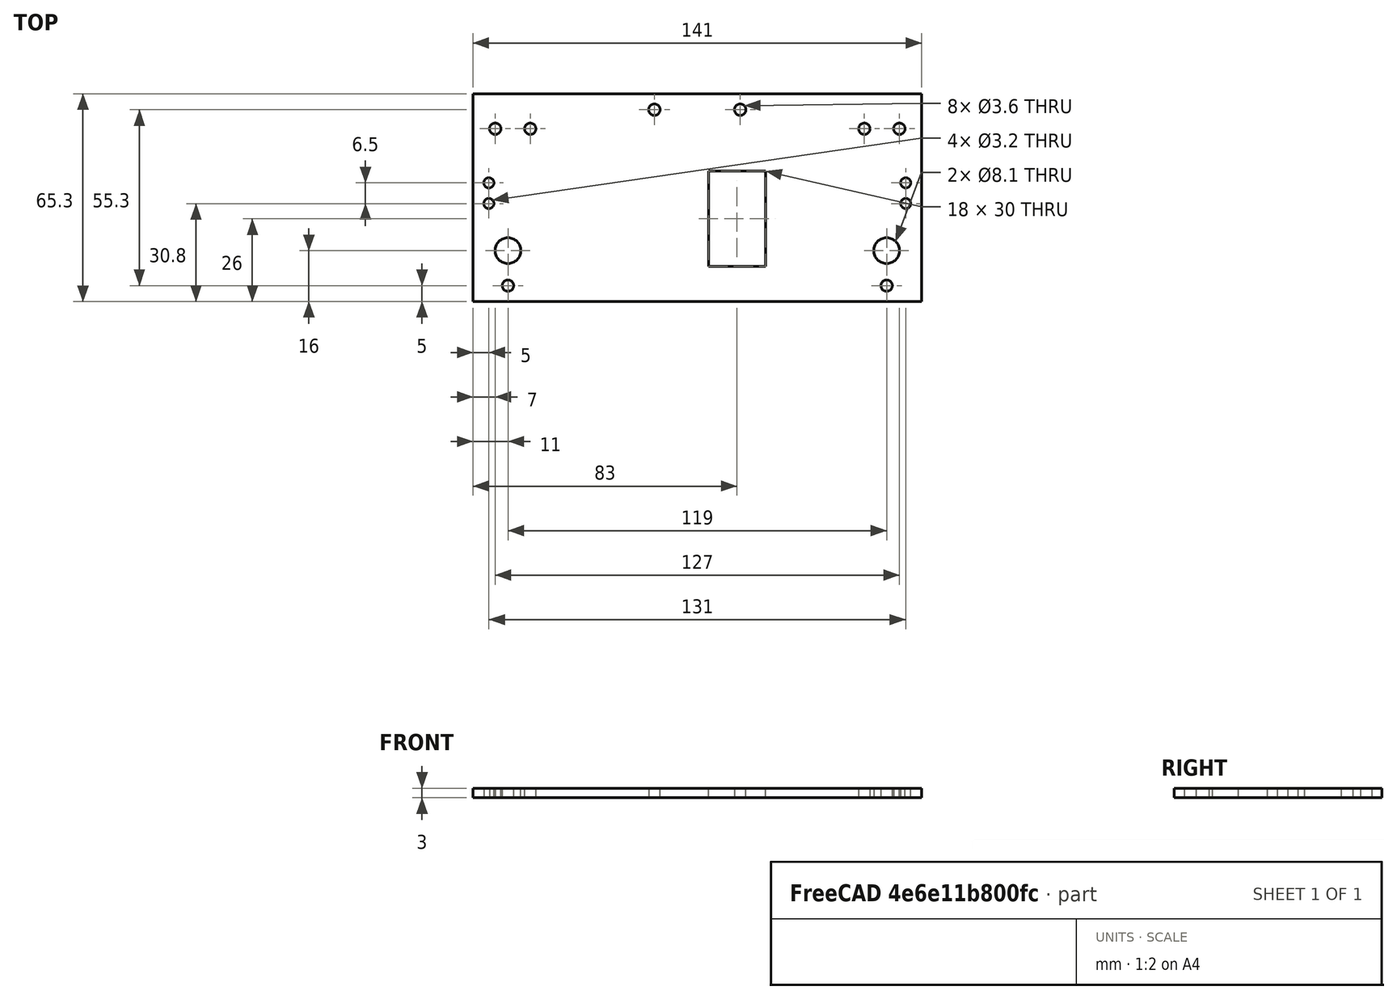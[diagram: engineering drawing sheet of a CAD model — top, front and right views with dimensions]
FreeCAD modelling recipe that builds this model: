
FCSTD DOCUMENT  (FreeCAD 0.16R6706 (Git))
Label: Plate Y Equerda
License: All rights reserved
LicenseURL: http://en.wikipedia.org/wiki/All_rights_reserved
objects: Path::FeaturePython×18, Sketcher::SketchObject×1, PartDesign::Pad×1, Path::FeatureCompoundPython×1
note: 3 computed .brp shape members not serialized (recipe doc carries the construction recipe); baked Part::Feature solids carry a one-line shape summary decoded from their .brp

FEATURE [Sketcher::SketchObject] Sketch
  sketch-geometry (30):
    g0: LineSegment StartX=-141 StartY=65.3 StartZ=0 EndX=0 EndY=65.3 EndZ=0
    g1: LineSegment StartX=0 StartY=65.3 StartZ=0 EndX=0 EndY=0 EndZ=0
    g2: LineSegment StartX=0 StartY=0 StartZ=0 EndX=-141 EndY=0 EndZ=0
    g3: LineSegment StartX=-141 StartY=0 StartZ=0 EndX=-141 EndY=65.3 EndZ=0
    g4: Circle CenterX=-130 CenterY=16 CenterZ=0 NormalX=0 NormalY=0 NormalZ=1 Radius=4.05
    g5: Circle CenterX=-11 CenterY=16 CenterZ=0 NormalX=0 NormalY=0 NormalZ=1 Radius=4.05
    g6: LineSegment [constr] StartX=-130 StartY=16 StartZ=0 EndX=-11 EndY=16 EndZ=0
    g7: LineSegment [constr] StartX=-134 StartY=54.3 StartZ=0 EndX=-123 EndY=54.3 EndZ=0
    g8: Circle CenterX=-134 CenterY=54.3 CenterZ=0 NormalX=0 NormalY=0 NormalZ=1 Radius=1.8
    g9: Circle CenterX=-123 CenterY=54.3 CenterZ=0 NormalX=0 NormalY=0 NormalZ=1 Radius=1.8
    g10: LineSegment [constr] StartX=-18 StartY=54.3 StartZ=0 EndX=-7 EndY=54.3 EndZ=0
    g11: Circle CenterX=-18 CenterY=54.3 CenterZ=0 NormalX=0 NormalY=0 NormalZ=1 Radius=1.8
    g12: Circle CenterX=-7 CenterY=54.3 CenterZ=0 NormalX=0 NormalY=0 NormalZ=1 Radius=1.8
    g13: LineSegment StartX=-67 StartY=41 StartZ=0 EndX=-49 EndY=41 EndZ=0
    g14: LineSegment StartX=-49 StartY=41 StartZ=0 EndX=-49 EndY=11 EndZ=0
    g15: LineSegment StartX=-49 StartY=11 StartZ=0 EndX=-67 EndY=11 EndZ=0
    g16: LineSegment StartX=-67 StartY=11 StartZ=0 EndX=-67 EndY=41 EndZ=0
    g17: LineSegment [constr] StartX=-5 StartY=37.3 StartZ=0 EndX=-5 EndY=30.8 EndZ=0
    g18: Circle CenterX=-5 CenterY=37.3 CenterZ=0 NormalX=0 NormalY=0 NormalZ=1 Radius=1.6
    g19: Circle CenterX=-5 CenterY=30.8 CenterZ=0 NormalX=0 NormalY=0 NormalZ=1 Radius=1.6
    g20: LineSegment [constr] StartX=-136 StartY=37.3 StartZ=0 EndX=-136 EndY=30.8 EndZ=0
    g21: Circle CenterX=-136 CenterY=37.3 CenterZ=0 NormalX=0 NormalY=0 NormalZ=1 Radius=1.6
    g22: Circle CenterX=-136 CenterY=30.8 CenterZ=0 NormalX=0 NormalY=0 NormalZ=1 Radius=1.6
    g23: LineSegment [constr] StartX=-84 StartY=60.3 StartZ=0 EndX=-57 EndY=60.3 EndZ=0
    g24: LineSegment [constr] StartX=-70.5 StartY=60.3 StartZ=0 EndX=-70.5 EndY=65.3 EndZ=0
    g25: Circle CenterX=-84 CenterY=60.3 CenterZ=0 NormalX=0 NormalY=0 NormalZ=1 Radius=1.8
    g26: Circle CenterX=-57 CenterY=60.3 CenterZ=0 NormalX=0 NormalY=0 NormalZ=1 Radius=1.8
    g27: LineSegment [constr] StartX=-130 StartY=5 StartZ=0 EndX=-11 EndY=5 EndZ=0
    g28: Circle CenterX=-130 CenterY=5 CenterZ=0 NormalX=0 NormalY=0 NormalZ=1 Radius=1.8
    g29: Circle CenterX=-11 CenterY=5 CenterZ=0 NormalX=0 NormalY=0 NormalZ=1 Radius=1.8
  constraints (82):
    c: Coincident(g0,g1)
    c: Coincident(g1,g2)
    c: Coincident(g2,g3)
    c: Coincident(g3,g0)
    c: Horizontal(g0)
    c: Horizontal(g2)
    c: Vertical(g1)
    c: Vertical(g3)
    c: Coincident(g1,g-1)
    c: Radius(g4) = 4.05
    c: Equal(g4,g5) = 4.3
    c: Horizontal(g6)
    c: Coincident(g4,g6)
    c: Coincident(g5,g6)
    c: DistanceX(g2,g4) = 11
    c: DistanceX(g5,g-1) = 11
    c: DistanceX(g6,g6) = 119
    c: DistanceY(g2,g4) = 16
    c: DistanceY(g4,g0) = 49.3
    c: DistanceY(g2,g0) = 65.3
    c: Horizontal(g7)
    c: DistanceX(g7,g7) = 11
    c: Radius(g8) = 1.8
    c: Equal(g8,g9) = 1.8
    c: Coincident(g7,g9)
    c: Coincident(g7,g8)
    c: Horizontal(g10)
    c: Equal(g7,g10) = 10
    c: Equal(g8,g11) = 1.8
    c: Equal(g11,g12) = 1.8
    c: Coincident(g10,g12)
    c: Coincident(g10,g11)
    c: DistanceY(g7,g0) = 11
    c: PointOnObject(g10,g7)
    c: DistanceX(g0,g7) = 7
    c: DistanceX(g10,g0) = 7
    c: Coincident(g13,g14)
    c: Coincident(g14,g15)
    c: Coincident(g15,g16)
    c: Coincident(g16,g13)
    c: Horizontal(g13)
    c: Horizontal(g15)
    c: Vertical(g14)
    c: Vertical(g16)
    c: Vertical(g17)
    c: DistanceY(g17,g17) = 6.5
    c: Radius(g18) = 1.6
    c: Equal(g18,g19) = 1.6
    c: Coincident(g17,g18)
    c: Coincident(g17,g19)
    c: Vertical(g20)
    c: Equal(g17,g20) = 6.5
    c: Equal(g18,g21) = 1.6
    c: Equal(g21,g22) = 1.6
    c: Coincident(g20,g21)
    c: Coincident(g20,g22)
    c: DistanceX(g17,g0) = 5
    c: DistanceX(g0,g20) = 5
    c: DistanceX(g15,g15) = 18
    c: DistanceY(g16,g16) = 30
    c: Horizontal(g23)
    c: DistanceX(g23,g23) = 27
    c: Vertical(g24)
    c: DistanceY(g24,g24) = 5
    c: Equal(g8,g25) = 1.8
    c: Equal(g8,g26) = 1.8
    c: Coincident(g23,g26)
    c: Coincident(g25,g23)
    c: Symmetric(g0,g0,g24)
    c: Symmetric(g23,g23,g24)
    c: DistanceY(g17,g0) = 28
    c: DistanceY(g20,g0) = 28
    c: DistanceY(g4,g13) = 25
    c: DistanceX(g14,g5) = 38
    c: Horizontal(g27)
    c: Equal(g6,g27) = 119
    c: DistanceY(g27,g4) = 11
    c: DistanceX(g2,g27) = 11
    c: Equal(g8,g28) = 1.8
    c: Coincident(g27,g28)
    c: Equal(g8,g29) = 1.8
    c: Coincident(g27,g29)
FEATURE [PartDesign::Pad] Pad
  Length = 3
  Length2 = 100
  Sketch = -> Sketch
  Type = 0
FEATURE [Path::FeaturePython] Machine  label="Machine_"  # Path/CAM operation (typed FeaturePython)
  MachineUnits = 0
  X = 0
  X_Max = 0
  X_Min = 0
  Y = 0
  Y_Max = 0
  Y_Min = 0
  Z = 0
  Z_Max = 0
  Z_Min = 0
FEATURE [Path::FeaturePython] Tool  label="Tool1"  # Path/CAM operation (typed FeaturePython)
  SpindleDir = 0
  SpindleSpeed = 0
  ToolNumber = 1
FEATURE [Path::FeaturePython] Profile  label="Berço"  # Path/CAM operation (typed FeaturePython)
  Active = true
  Base = -> Pad
  ClearanceHeight = 3
  Direction = 1
  Edge1 = -> Pad [Edge42]
  EndPoint = (0,0,0)
  ExtendAtEnd = 0
  ExtendAtStart = 0
  FinalDepth = -5.1
  HorizFeed = 127
  LeadInLineLen = 0
  LeadOutLineLen = 0
  OffsetExtra = 0
  PathClosed = true
  RetractHeight = 0
  RollRadius = 0
  SegLen = 0.5
  Side = 1
  StartDepth = 0
  StartPoint = (0,0,0)
  StepDown = 2
  ToolNumber = 1
  UseEndPoint = false
  UsePlacements = false
  UseStartDepth = true
  UseStartPoint = false
  VertFeed = 127
FEATURE [Path::FeaturePython] Profile001  label="Berço001"  # Path/CAM operation (typed FeaturePython)
  Active = true
  Base = -> Pad
  ClearanceHeight = 3
  Direction = 1
  Edge1 = -> Pad [Edge39]
  EndPoint = (0,0,0)
  ExtendAtEnd = 0
  ExtendAtStart = 0
  FinalDepth = -5.1
  HorizFeed = 127
  LeadInLineLen = 0
  LeadOutLineLen = 0
  OffsetExtra = 0
  PathClosed = true
  RetractHeight = 0
  RollRadius = 0
  SegLen = 0.5
  Side = 1
  StartDepth = 0
  StartPoint = (0,0,0)
  StepDown = 2
  ToolNumber = 1
  UseEndPoint = false
  UsePlacements = false
  UseStartDepth = true
  UseStartPoint = false
  VertFeed = 127
FEATURE [Path::FeaturePython] Profile002  label="Berço002"  # Path/CAM operation (typed FeaturePython)
  Active = true
  Base = -> Pad
  ClearanceHeight = 3
  Direction = 1
  Edge1 = -> Pad [Edge51]
  EndPoint = (0,0,0)
  ExtendAtEnd = 0
  ExtendAtStart = 0
  FinalDepth = -5.1
  HorizFeed = 127
  LeadInLineLen = 0
  LeadOutLineLen = 0
  OffsetExtra = 0
  PathClosed = true
  RetractHeight = 0
  RollRadius = 0
  SegLen = 0.5
  Side = 1
  StartDepth = 0
  StartPoint = (0,0,0)
  StepDown = 2
  ToolNumber = 1
  UseEndPoint = false
  UsePlacements = false
  UseStartDepth = true
  UseStartPoint = false
  VertFeed = 127
FEATURE [Path::FeaturePython] Profile003  label="Berço003"  # Path/CAM operation (typed FeaturePython)
  Active = true
  Base = -> Pad
  ClearanceHeight = 3
  Direction = 1
  Edge1 = -> Pad [Edge48]
  EndPoint = (0,0,0)
  ExtendAtEnd = 0
  ExtendAtStart = 0
  FinalDepth = -5.1
  HorizFeed = 127
  LeadInLineLen = 0
  LeadOutLineLen = 0
  OffsetExtra = 0
  PathClosed = true
  RetractHeight = 0
  RollRadius = 0
  SegLen = 0.5
  Side = 1
  StartDepth = 0
  StartPoint = (0,0,0)
  StepDown = 2
  ToolNumber = 1
  UseEndPoint = false
  UsePlacements = false
  UseStartDepth = true
  UseStartPoint = false
  VertFeed = 127
FEATURE [Path::FeaturePython] Profile004  label="suporte correia"  # Path/CAM operation (typed FeaturePython)
  Active = true
  Base = -> Pad
  ClearanceHeight = 3
  Direction = 1
  Edge1 = -> Pad [Edge36]
  EndPoint = (0,0,0)
  ExtendAtEnd = 0
  ExtendAtStart = 0
  FinalDepth = -5.1
  HorizFeed = 127
  LeadInLineLen = 0
  LeadOutLineLen = 0
  OffsetExtra = 0
  PathClosed = true
  RetractHeight = 0
  RollRadius = 0
  SegLen = 0.5
  Side = 1
  StartDepth = 0
  StartPoint = (0,0,0)
  StepDown = 2
  ToolNumber = 1
  UseEndPoint = false
  UsePlacements = false
  UseStartDepth = true
  UseStartPoint = false
  VertFeed = 127
FEATURE [Path::FeaturePython] Profile005  label="suporte correia001"  # Path/CAM operation (typed FeaturePython)
  Active = true
  Base = -> Pad
  ClearanceHeight = 3
  Direction = 1
  Edge1 = -> Pad [Edge33]
  EndPoint = (0,0,0)
  ExtendAtEnd = 0
  ExtendAtStart = 0
  FinalDepth = -5.1
  HorizFeed = 127
  LeadInLineLen = 0
  LeadOutLineLen = 0
  OffsetExtra = 0
  PathClosed = true
  RetractHeight = 0
  RollRadius = 0
  SegLen = 0.5
  Side = 1
  StartDepth = 0
  StartPoint = (0,0,0)
  StepDown = 2
  ToolNumber = 1
  UseEndPoint = false
  UsePlacements = false
  UseStartDepth = true
  UseStartPoint = false
  VertFeed = 127
FEATURE [Path::FeaturePython] Profile006  label="EndStop"  # Path/CAM operation (typed FeaturePython)
  Active = true
  Base = -> Pad
  ClearanceHeight = 3
  Direction = 1
  Edge1 = -> Pad [Edge66]
  EndPoint = (0,0,0)
  ExtendAtEnd = 0
  ExtendAtStart = 0
  FinalDepth = -5.1
  HorizFeed = 127
  LeadInLineLen = 0
  LeadOutLineLen = 0
  OffsetExtra = 0
  PathClosed = true
  RetractHeight = 0
  RollRadius = 0
  SegLen = 0.5
  Side = 1
  StartDepth = 0
  StartPoint = (0,0,0)
  StepDown = 2
  ToolNumber = 1
  UseEndPoint = false
  UsePlacements = false
  UseStartDepth = true
  UseStartPoint = false
  VertFeed = 127
FEATURE [Path::FeaturePython] Profile007  label="EndStop001"  # Path/CAM operation (typed FeaturePython)
  Active = true
  Base = -> Pad
  ClearanceHeight = 3
  Direction = 1
  Edge1 = -> Pad [Edge63]
  EndPoint = (0,0,0)
  ExtendAtEnd = 0
  ExtendAtStart = 0
  FinalDepth = -5.1
  HorizFeed = 127
  LeadInLineLen = 0
  LeadOutLineLen = 0
  OffsetExtra = 0
  PathClosed = true
  RetractHeight = 0
  RollRadius = 0
  SegLen = 0.5
  Side = 1
  StartDepth = 0
  StartPoint = (0,0,0)
  StepDown = 2
  ToolNumber = 1
  UseEndPoint = false
  UsePlacements = false
  UseStartDepth = true
  UseStartPoint = false
  VertFeed = 127
FEATURE [Path::FeaturePython] Profile008  label="EndStop002"  # Path/CAM operation (typed FeaturePython)
  Active = true
  Base = -> Pad
  ClearanceHeight = 3
  Direction = 1
  Edge1 = -> Pad [Edge60]
  EndPoint = (0,0,0)
  ExtendAtEnd = 0
  ExtendAtStart = 0
  FinalDepth = -5.1
  HorizFeed = 127
  LeadInLineLen = 0
  LeadOutLineLen = 0
  OffsetExtra = 0
  PathClosed = true
  RetractHeight = 0
  RollRadius = 0
  SegLen = 0.5
  Side = 1
  StartDepth = 0
  StartPoint = (0,0,0)
  StepDown = 2
  ToolNumber = 1
  UseEndPoint = false
  UsePlacements = false
  UseStartDepth = true
  UseStartPoint = false
  VertFeed = 127
FEATURE [Path::FeaturePython] Profile009  label="EndStop003"  # Path/CAM operation (typed FeaturePython)
  Active = true
  Base = -> Pad
  ClearanceHeight = 3
  Direction = 1
  Edge1 = -> Pad [Edge57]
  EndPoint = (0,0,0)
  ExtendAtEnd = 0
  ExtendAtStart = 0
  FinalDepth = -5.1
  HorizFeed = 127
  LeadInLineLen = 0
  LeadOutLineLen = 0
  OffsetExtra = 0
  PathClosed = true
  RetractHeight = 0
  RollRadius = 0
  SegLen = 0.5
  Side = 1
  StartDepth = 0
  StartPoint = (0,0,0)
  StepDown = 2
  ToolNumber = 1
  UseEndPoint = false
  UsePlacements = false
  UseStartDepth = true
  UseStartPoint = false
  VertFeed = 127
FEATURE [Path::FeaturePython] Profile010  label="Eixo"  # Path/CAM operation (typed FeaturePython)
  Active = true
  Base = -> Pad
  ClearanceHeight = 3
  Direction = 1
  Edge1 = -> Pad [Edge27]
  EndPoint = (0,0,0)
  ExtendAtEnd = 0
  ExtendAtStart = 0
  FinalDepth = -5.1
  HorizFeed = 127
  LeadInLineLen = 0
  LeadOutLineLen = 0
  OffsetExtra = 0
  PathClosed = true
  RetractHeight = 0
  RollRadius = 0
  SegLen = 0.5
  Side = 1
  StartDepth = 0
  StartPoint = (0,0,0)
  StepDown = 2
  ToolNumber = 1
  UseEndPoint = false
  UsePlacements = false
  UseStartDepth = true
  UseStartPoint = false
  VertFeed = 127
FEATURE [Path::FeaturePython] Profile011  label="Eixo001"  # Path/CAM operation (typed FeaturePython)
  Active = true
  Base = -> Pad
  ClearanceHeight = 3
  Direction = 1
  Edge1 = -> Pad [Edge30]
  EndPoint = (0,0,0)
  ExtendAtEnd = 0
  ExtendAtStart = 0
  FinalDepth = -5.1
  HorizFeed = 127
  LeadInLineLen = 0
  LeadOutLineLen = 0
  OffsetExtra = 0
  PathClosed = true
  RetractHeight = 0
  RollRadius = 0
  SegLen = 0.5
  Side = 1
  StartDepth = 0
  StartPoint = (0,0,0)
  StepDown = 2
  ToolNumber = 1
  UseEndPoint = false
  UsePlacements = false
  UseStartDepth = true
  UseStartPoint = false
  VertFeed = 127
FEATURE [Path::FeaturePython] Profile012  label="Fixacao"  # Path/CAM operation (typed FeaturePython)
  Active = true
  Base = -> Pad
  ClearanceHeight = 3
  Direction = 1
  Edge1 = -> Pad [Edge45]
  EndPoint = (0,0,0)
  ExtendAtEnd = 0
  ExtendAtStart = 0
  FinalDepth = -5.1
  HorizFeed = 127
  LeadInLineLen = 0
  LeadOutLineLen = 0
  OffsetExtra = 0
  PathClosed = true
  RetractHeight = 0
  RollRadius = 0
  SegLen = 0.5
  Side = 1
  StartDepth = 0
  StartPoint = (0,0,0)
  StepDown = 2
  ToolNumber = 1
  UseEndPoint = false
  UsePlacements = false
  UseStartDepth = true
  UseStartPoint = false
  VertFeed = 127
FEATURE [Path::FeaturePython] Profile013  label="Fixacao001"  # Path/CAM operation (typed FeaturePython)
  Active = true
  Base = -> Pad
  ClearanceHeight = 3
  Direction = 1
  Edge1 = -> Pad [Edge54]
  EndPoint = (0,0,0)
  ExtendAtEnd = 0
  ExtendAtStart = 0
  FinalDepth = -5.1
  HorizFeed = 127
  LeadInLineLen = 0
  LeadOutLineLen = 0
  OffsetExtra = 0
  PathClosed = true
  RetractHeight = 0
  RollRadius = 0
  SegLen = 0.5
  Side = 1
  StartDepth = 0
  StartPoint = (0,0,0)
  StepDown = 2
  ToolNumber = 1
  UseEndPoint = false
  UsePlacements = false
  UseStartDepth = true
  UseStartPoint = false
  VertFeed = 127
FEATURE [Path::FeaturePython] Profile014  label="Janela"  # Path/CAM operation (typed FeaturePython)
  Active = true
  Base = -> Pad
  ClearanceHeight = 3
  Direction = 1
  Edge1 = -> Pad [Edge24]
  Edge2 = -> Pad [Edge22]
  EndPoint = (0,0,0)
  ExtendAtEnd = 0
  ExtendAtStart = 0
  FinalDepth = -5.1
  HorizFeed = 127
  LeadInLineLen = 0
  LeadOutLineLen = 0
  OffsetExtra = 0
  PathClosed = true
  RetractHeight = 0
  RollRadius = 0
  SegLen = 0.5
  Side = 1
  StartDepth = 0
  StartPoint = (0,0,0)
  StepDown = 2
  ToolNumber = 1
  UseEndPoint = false
  UsePlacements = false
  UseStartDepth = true
  UseStartPoint = false
  VertFeed = 127
FEATURE [Path::FeaturePython] Profile015  label="Externo"  # Path/CAM operation (typed FeaturePython)
  Active = true
  Base = -> Pad
  ClearanceHeight = 3
  Direction = 0
  EndPoint = (0,0,0)
  ExtendAtEnd = 0
  ExtendAtStart = 0
  Face1 = -> Pad [Face24]
  FinalDepth = -5.1
  HorizFeed = 127
  LeadInLineLen = 0
  LeadOutLineLen = 0
  OffsetExtra = 0
  PathClosed = true
  RetractHeight = 0
  RollRadius = 0
  SegLen = 0.5
  Side = 0
  StartDepth = 0
  StartPoint = (0,0,0)
  StepDown = 2
  ToolNumber = 1
  UseEndPoint = false
  UsePlacements = false
  UseStartDepth = true
  UseStartPoint = false
  VertFeed = 127
FEATURE [Path::FeatureCompoundPython] Project  # Path/CAM operation (typed FeaturePython)
  Group = -> [Machine,Tool,Profile,Profile001,Profile002,Profile003,Profile004,Profile005,Profile006,Profile007,Profile008,Profile009,Profile010,Profile011,Profile012,Profile013,Profile014,Profile015]
  UsePlacements = false
